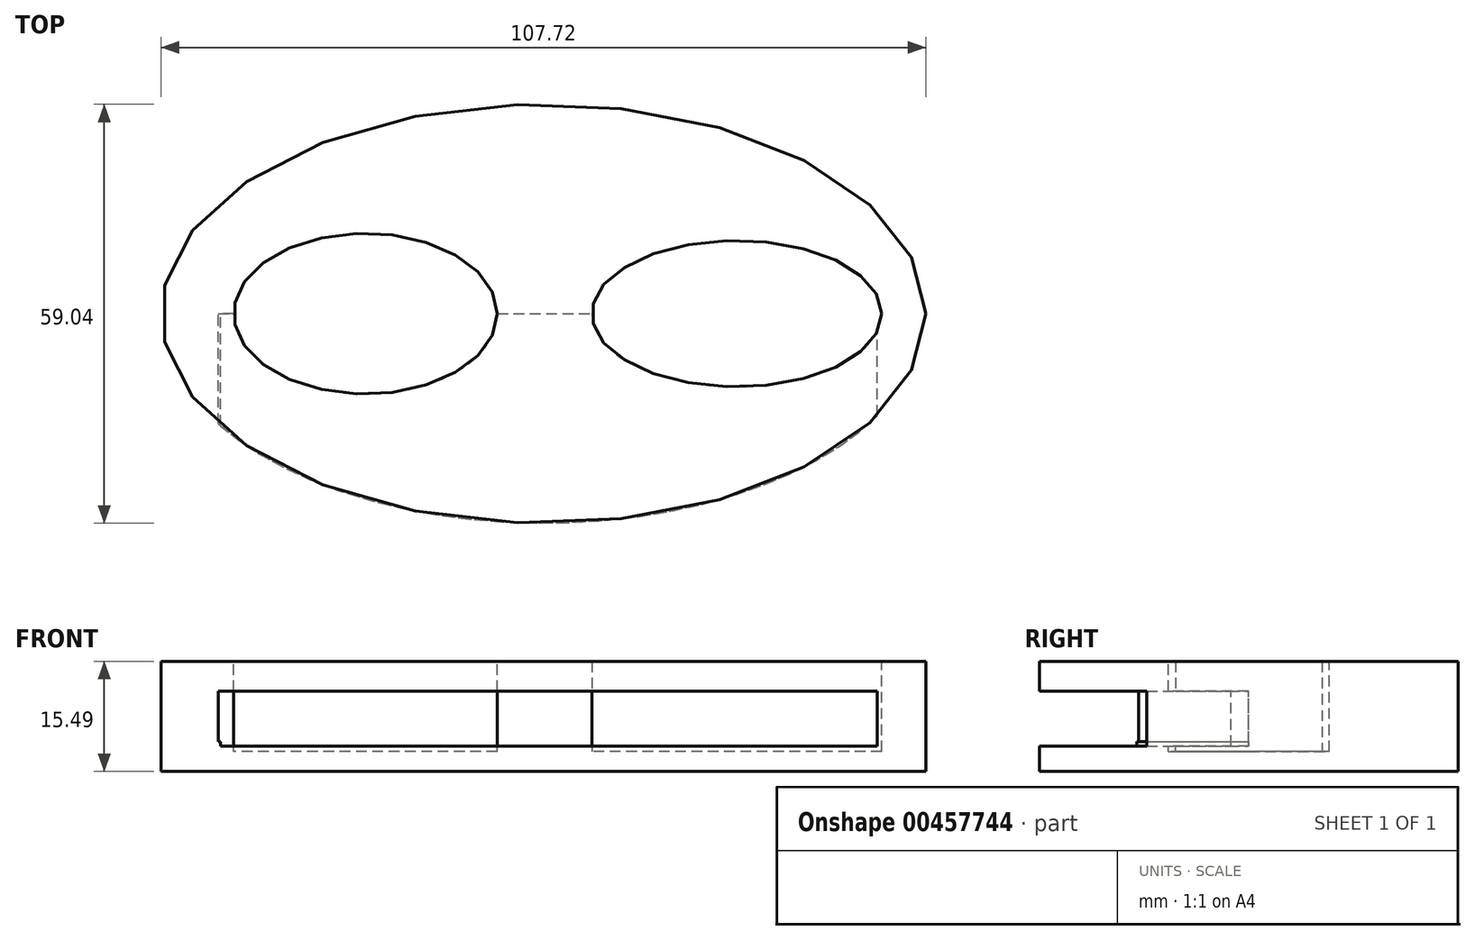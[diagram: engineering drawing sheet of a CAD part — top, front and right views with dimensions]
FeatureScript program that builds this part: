
annotation { "Feature Type Name" : "Feature", "Feature Type Description" : "" }
export const myFeature = defineFeature(function(context is Context, id is Id, definition is map)
    precondition{}
    {
        {
            var Q0;
            Q0=qCreatedBy(makeId("Top.planeOp"),FACE);
            var sketch = newSketch(context, id + "F0", { "sketchPlane" : qUnion([Q0])});
            skEllipse(sketch, "E0", {"center": v(0, 0) * mm, "majorRadius": 53.86 * mm, "minorRadius": 29.52 * mm, "majorAxis": v(1, 0)});
            skSolve(sketch);
        }
        {
            var Q0;
            Q0 = qSketchRegion(id + "F0", true);
            extrude(context, id + "F1", {"entities" : qUnion([Q0]), "depth" : 15.5 * mm});
        }
        {
            var Q0;
            Q0=makeQuery(id+"F1.opExtrude","CAP_FACE",FACE,{"disambiguationData":[OSD([sQuery(id+"F0.wireOp",EDGE,"E0")])],"isStart":false});
            var sketch = newSketch(context, id + "F2", { "sketchPlane" : qUnion([Q0])});
            skEllipse(sketch, "E1", {"center": v(-25.07, 0) * mm, "majorRadius": 18.57 * mm, "minorRadius": 11.33 * mm, "majorAxis": v(1, 0)});
            skEllipse(sketch, "E2", {"center": v(27.24, 0) * mm, "majorRadius": 20.43 * mm, "minorRadius": 10.3 * mm, "majorAxis": v(1, 0)});
            skSolve(sketch);
        }
        {
            var Q0;
            Q0=makeQuery(id+"F2.imprint","IMPRINT",FACE,{"disambiguationData":[TD([[makeQuery(id+"F2.imprint","IMPRINT",EDGE,{"derivedFrom":sQuery(id+"F2.wireOp",EDGE,"E1")}),1.0]])]});
            var Q1;
            Q1=makeQuery(id+"F2.imprint","IMPRINT",FACE,{"disambiguationData":[TD([[makeQuery(id+"F2.imprint","IMPRINT",EDGE,{"derivedFrom":sQuery(id+"F2.wireOp",EDGE,"E2")}),1.0]])]});
            var Q2;
            Q2=sQuery(id+"F2.wireOp",EDGE,"E2");
            var Q3;
            Q3=sQuery(id+"F2.wireOp",EDGE,"E1");
            extrude(context, id + "F3", {"entities" : qUnion([Q0, Q1]), "operationType" : NewBodyOperationType.REMOVE, "surfaceEntities" : qUnion([Q2, Q3]), "oppositeDirection" : true, "depth" : 12.7 * mm});
        }
        {
            var Q0;
            Q0=qCreatedBy(makeId("Front.planeOp"),FACE);
            var sketch = newSketch(context, id + "F4", { "sketchPlane" : qUnion([Q0])});
            skLineSegment(sketch, "E3.bottom", {"start": v(-45.8, 4.18) * mm, "end": v(47.05, 4.18) * mm});
            skLineSegment(sketch, "E3.top", {"start": v(-45.8, 11.3) * mm, "end": v(47.05, 11.3) * mm});
            skLineSegment(sketch, "E3.left", {"start": v(-45.8, 4.18) * mm, "end": v(-45.8, 11.3) * mm});
            skLineSegment(sketch, "E3.right", {"start": v(47.05, 4.18) * mm, "end": v(47.05, 11.3) * mm});
            skSolve(sketch);
        }
        {
            var Q0;
            Q0 = qSketchRegion(id + "F4", true);
            extrude(context, id + "F5", {"entities" : qUnion([Q0]), "operationType" : NewBodyOperationType.REMOVE, "depth" : 21.59 * mm});
        }
        {
            var Q0;
            Q0=qCreatedBy(makeId("Front.planeOp"),FACE);
            var sketch = newSketch(context, id + "F6", { "sketchPlane" : qUnion([Q0])});
            skLineSegment(sketch, "E4.bottom", {"start": v(47.05, 11.3) * mm, "end": v(-45.5, 11.3) * mm});
            skLineSegment(sketch, "E4.top", {"start": v(47.05, 3.56) * mm, "end": v(-45.5, 3.56) * mm});
            skLineSegment(sketch, "E4.left", {"start": v(47.05, 11.3) * mm, "end": v(47.05, 3.56) * mm});
            skLineSegment(sketch, "E4.right", {"start": v(-45.5, 11.3) * mm, "end": v(-45.5, 3.56) * mm});
            skSolve(sketch);
        }
        {
            var Q0;
            Q0 = qSketchRegion(id + "F6", true);
            extrude(context, id + "F7", {"entities" : qUnion([Q0]), "operationType" : NewBodyOperationType.REMOVE, "depth" : 50.8 * mm});
        }
    });
